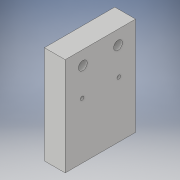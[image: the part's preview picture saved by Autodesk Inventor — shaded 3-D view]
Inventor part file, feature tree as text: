
AUTODESK INVENTOR PART (.ipt)
format: ipt  version: 2017 (Build 210142000, 142)  size: 112,640 bytes
history: native  units: in
note: dims shown in document units (in); Inventor stores cm internally (conversion verified against a paired STEP export)
features: extrude x1, sketch x1
ambient origin geometry x8: Origin, YZ Plane, XZ Plane, XY Plane, X Axis, Y Axis, Z Axis, Center Point
bodies: Solid1 (feature_tree)
feature tree (2):
  extrude  "Extrusion1"  Depth=1.0in
  sketch  "Sketch1"  dims[d0=0.3937in d1=1.0in d2=0.25in d3=0.25in d4=0.125in d5=0.125in d6=0.5in d7=0.74in d8=0.7in d9=0.67in d10=0.09in d11=0.05in d12=0.2953in d13=0.0in]
